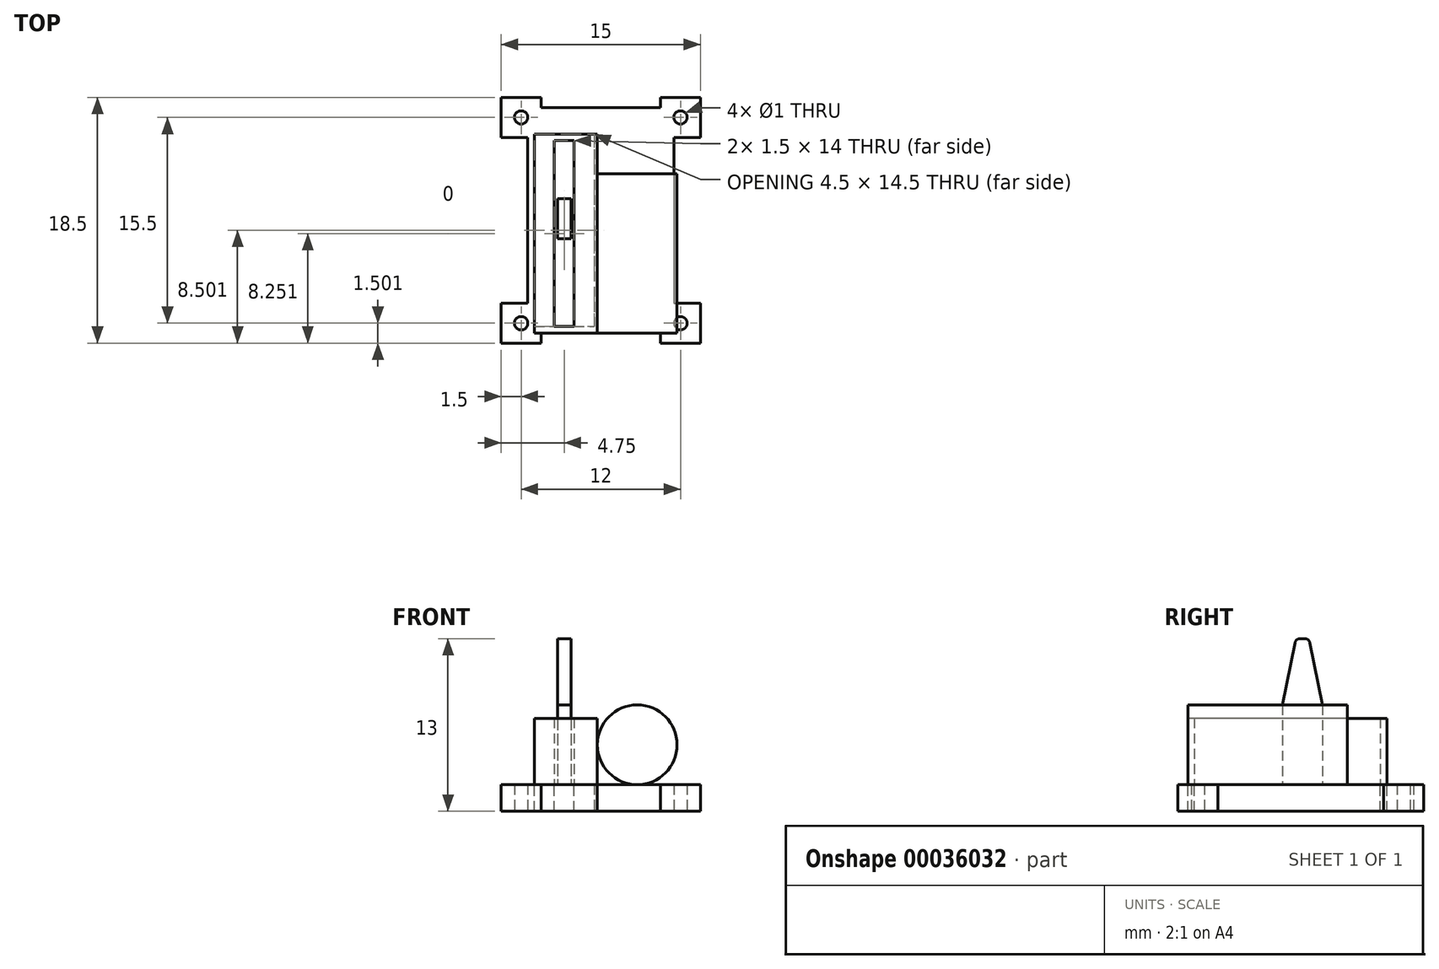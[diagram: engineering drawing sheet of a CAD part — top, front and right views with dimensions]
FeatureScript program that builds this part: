
annotation { "Feature Type Name" : "Feature", "Feature Type Description" : "" }
export const myFeature = defineFeature(function(context is Context, id is Id, definition is map)
    precondition{}
    {
        {
            var Q0;
            Q0=qCreatedBy(makeId("Top.planeOp"),FACE);
            var sketch = newSketch(context, id + "F0", { "sketchPlane" : qUnion([Q0])});
            skLineSegment(sketch, "E0.bottom", {"start": v(-5.24, 11.28) * mm, "end": v(5.76, 11.28) * mm, "construction": true});
            skLineSegment(sketch, "E0.top", {"start": v(-5.24, -5.72) * mm, "end": v(5.76, -5.72) * mm, "construction": true});
            skLineSegment(sketch, "E0.left", {"start": v(-5.24, 11.28) * mm, "end": v(-5.24, -5.22) * mm, "construction": true});
            skLineSegment(sketch, "E0.right", {"start": v(5.76, 11.28) * mm, "end": v(5.76, -5.72) * mm, "construction": true});
            skLineSegment(sketch, "E1.bottom", {"start": v(-7.24, 12.03) * mm, "end": v(7.76, 12.03) * mm, "construction": true});
            skLineSegment(sketch, "E1.top", {"start": v(-7.24, -6.47) * mm, "end": v(7.76, -6.47) * mm, "construction": true});
            skLineSegment(sketch, "E1.left", {"start": v(-7.24, 12.03) * mm, "end": v(-7.24, -6.47) * mm, "construction": true});
            skLineSegment(sketch, "E1.right", {"start": v(7.76, 12.03) * mm, "end": v(7.76, -6.47) * mm, "construction": true});
            skLineSegment(sketch, "E2.bottom", {"start": v(7.76, 12.03) * mm, "end": v(4.76, 12.03) * mm, "construction": true});
            skLineSegment(sketch, "E2.top", {"start": v(7.76, 9.03) * mm, "end": v(4.76, 9.03) * mm, "construction": true});
            skLineSegment(sketch, "E2.left", {"start": v(7.76, 12.03) * mm, "end": v(7.76, 9.03) * mm, "construction": true});
            skLineSegment(sketch, "E2.right", {"start": v(4.76, 12.03) * mm, "end": v(4.76, 9.03) * mm, "construction": true});
            skLineSegment(sketch, "E3.bottom", {"start": v(-7.24, 12.03) * mm, "end": v(-4.24, 12.03) * mm, "construction": true});
            skLineSegment(sketch, "E3.top", {"start": v(-7.24, 9.03) * mm, "end": v(-4.24, 9.03) * mm, "construction": true});
            skLineSegment(sketch, "E3.left", {"start": v(-7.24, 12.03) * mm, "end": v(-7.24, 9.03) * mm, "construction": true});
            skLineSegment(sketch, "E3.right", {"start": v(-4.24, 12.03) * mm, "end": v(-4.24, 9.03) * mm, "construction": true});
            skLineSegment(sketch, "E4.bottom", {"start": v(-7.24, -6.47) * mm, "end": v(-4.24, -6.47) * mm, "construction": true});
            skLineSegment(sketch, "E4.top", {"start": v(-7.24, -3.47) * mm, "end": v(-4.24, -3.47) * mm, "construction": true});
            skLineSegment(sketch, "E4.left", {"start": v(-7.24, -6.47) * mm, "end": v(-7.24, -3.47) * mm, "construction": true});
            skLineSegment(sketch, "E4.right", {"start": v(-4.24, -6.47) * mm, "end": v(-4.24, -3.47) * mm, "construction": true});
            skLineSegment(sketch, "E5.bottom", {"start": v(7.76, -6.47) * mm, "end": v(4.76, -6.47) * mm, "construction": true});
            skLineSegment(sketch, "E5.top", {"start": v(7.76, -3.47) * mm, "end": v(4.76, -3.47) * mm, "construction": true});
            skLineSegment(sketch, "E5.left", {"start": v(7.76, -6.47) * mm, "end": v(7.76, -3.47) * mm, "construction": true});
            skLineSegment(sketch, "E5.right", {"start": v(4.76, -6.47) * mm, "end": v(4.76, -3.47) * mm, "construction": true});
            skLineSegment(sketch, "E6", {"start": v(-7.24, 12.03) * mm, "end": v(-4.24, 12.03) * mm});
            skLineSegment(sketch, "E7", {"start": v(-4.24, 11.28) * mm, "end": v(4.76, 11.28) * mm});
            skLineSegment(sketch, "E8", {"start": v(4.76, 11.28) * mm, "end": v(4.76, 12.03) * mm});
            skLineSegment(sketch, "E9", {"start": v(7.76, 12.03) * mm, "end": v(7.76, 9.03) * mm});
            skLineSegment(sketch, "E10", {"start": v(4.76, 12.03) * mm, "end": v(7.76, 12.03) * mm});
            skLineSegment(sketch, "E11", {"start": v(7.76, 9.03) * mm, "end": v(5.76, 9.03) * mm});
            skLineSegment(sketch, "E12", {"start": v(5.76, 9.03) * mm, "end": v(5.76, -3.47) * mm});
            skLineSegment(sketch, "E13", {"start": v(5.76, -3.47) * mm, "end": v(7.76, -3.47) * mm});
            skLineSegment(sketch, "E14", {"start": v(7.76, -3.47) * mm, "end": v(7.76, -6.47) * mm});
            skLineSegment(sketch, "E15", {"start": v(7.76, -6.47) * mm, "end": v(4.76, -6.47) * mm});
            skLineSegment(sketch, "E16", {"start": v(4.76, -5.72) * mm, "end": v(4.76, -6.47) * mm});
            skLineSegment(sketch, "E17", {"start": v(4.76, -5.72) * mm, "end": v(-4.24, -5.72) * mm});
            skLineSegment(sketch, "E18", {"start": v(-4.24, -6.47) * mm, "end": v(-4.24, -5.72) * mm});
            skLineSegment(sketch, "E19", {"start": v(-4.24, -6.47) * mm, "end": v(-7.24, -6.47) * mm});
            skLineSegment(sketch, "E20", {"start": v(-7.24, -3.47) * mm, "end": v(-7.24, -6.47) * mm});
            skLineSegment(sketch, "E21", {"start": v(-7.24, -3.47) * mm, "end": v(-5.24, -3.47) * mm});
            skLineSegment(sketch, "E22", {"start": v(-5.24, -3.47) * mm, "end": v(-5.24, 9.03) * mm});
            skLineSegment(sketch, "E23", {"start": v(-5.24, 9.03) * mm, "end": v(-7.24, 9.03) * mm});
            skLineSegment(sketch, "E24", {"start": v(-7.24, 12.03) * mm, "end": v(-7.24, 9.03) * mm});
            skLineSegment(sketch, "E25", {"start": v(-4.24, 12.03) * mm, "end": v(-4.24, 11.28) * mm});
            skLineSegment(sketch, "E26", {"start": v(7.76, 12.03) * mm, "end": v(4.76, 9.03) * mm, "construction": true});
            skLineSegment(sketch, "E27", {"start": v(-7.24, 12.03) * mm, "end": v(-4.24, 9.03) * mm, "construction": true});
            skLineSegment(sketch, "E28", {"start": v(-4.24, -3.47) * mm, "end": v(-7.24, -6.47) * mm, "construction": true});
            skLineSegment(sketch, "E29", {"start": v(4.76, -3.47) * mm, "end": v(7.76, -6.47) * mm, "construction": true});
            skCircle(sketch, "E30", {"center": v(6.26, 10.53) * mm, "radius": 0.5 * mm});
            skCircle(sketch, "E31", {"center": v(-5.74, 10.53) * mm, "radius": 0.5 * mm});
            skCircle(sketch, "E32", {"center": v(6.26, -4.97) * mm, "radius": 0.5 * mm});
            skCircle(sketch, "E33", {"center": v(-5.74, -4.97) * mm, "radius": 0.5 * mm});
            skLineSegment(sketch, "E34.bottom", {"start": v(-4.74, 9.28) * mm, "end": v(-0.24, 9.28) * mm});
            skLineSegment(sketch, "E34.top", {"start": v(-4.74, -5.72) * mm, "end": v(-0.24, -5.72) * mm});
            skLineSegment(sketch, "E34.left", {"start": v(-4.74, 9.28) * mm, "end": v(-4.74, -5.72) * mm});
            skLineSegment(sketch, "E34.right", {"start": v(-0.24, 9.28) * mm, "end": v(-0.24, -5.72) * mm});
            skLineSegment(sketch, "E35.bottom", {"start": v(-3.24, 8.78) * mm, "end": v(-1.74, 8.78) * mm});
            skLineSegment(sketch, "E35.top", {"start": v(-3.24, -5.22) * mm, "end": v(-1.74, -5.22) * mm});
            skLineSegment(sketch, "E35.left", {"start": v(-3.24, 8.78) * mm, "end": v(-3.24, -5.22) * mm});
            skLineSegment(sketch, "E35.right", {"start": v(-1.74, 8.78) * mm, "end": v(-1.74, -5.22) * mm});
            skLineSegment(sketch, "E36", {"start": v(-4.74, -5.22) * mm, "end": v(-0.24, -5.22) * mm});
            skSolve(sketch);
        }
        {
            var Q0;
            {var subQ7=sQuery(id+"F0.wireOp",EDGE,"E34.top");var subQ10=makeQuery(id+"F0.imprint","INTERSECT",VERTEX,{"derivedFrom":[sQuery(id+"F0.wireOp",EDGE,"E18"),subQ7]});Q0=makeQuery(id+"F0.imprint","IMPRINT",FACE,{"disambiguationData":[TD([[makeQuery(id+"F0.imprint","IMPRINT",EDGE,{"disambiguationData":[TD([[subQ10,1.0]])],"derivedFrom":subQ7}),1.0]])]});}
            var Q1;
            Q1=makeQuery(id+"F0.imprint","IMPRINT",FACE,{"disambiguationData":[TD([[makeQuery(id+"F0.imprint","IMPRINT",EDGE,{"derivedFrom":sQuery(id+"F0.wireOp",EDGE,"E6")}),-1.0]])]});
            var Q2;
            Q2=makeQuery(id+"F0.imprint","IMPRINT",FACE,{"disambiguationData":[TD([[makeQuery(id+"F0.imprint","IMPRINT",EDGE,{"derivedFrom":sQuery(id+"F0.wireOp",EDGE,"E35.bottom")}),-1.0]])]});
            extrude(context, id + "F1", {"entities" : qUnion([Q0, Q1, Q2]), "depth" : 2 * mm});
        }
        {
            var Q0;
            Q0=makeQuery(id+"F1.opExtrude","CAP_FACE",FACE,{"disambiguationData":[OSD([sQuery(id+"F0.wireOp",EDGE,"E6"),sQuery(id+"F0.wireOp",EDGE,"E7"),sQuery(id+"F0.wireOp",EDGE,"E8"),sQuery(id+"F0.wireOp",EDGE,"E9"),sQuery(id+"F0.wireOp",EDGE,"E10"),sQuery(id+"F0.wireOp",EDGE,"E11"),sQuery(id+"F0.wireOp",EDGE,"E12"),sQuery(id+"F0.wireOp",EDGE,"E13"),sQuery(id+"F0.wireOp",EDGE,"E14"),sQuery(id+"F0.wireOp",EDGE,"E15"),sQuery(id+"F0.wireOp",EDGE,"E16"),sQuery(id+"F0.wireOp",EDGE,"E17"),sQuery(id+"F0.wireOp",EDGE,"E18"),sQuery(id+"F0.wireOp",EDGE,"E19"),sQuery(id+"F0.wireOp",EDGE,"E20"),sQuery(id+"F0.wireOp",EDGE,"E21"),sQuery(id+"F0.wireOp",EDGE,"E22"),sQuery(id+"F0.wireOp",EDGE,"E23"),sQuery(id+"F0.wireOp",EDGE,"E24"),sQuery(id+"F0.wireOp",EDGE,"E25"),sQuery(id+"F0.wireOp",EDGE,"E30"),sQuery(id+"F0.wireOp",EDGE,"E31"),sQuery(id+"F0.wireOp",EDGE,"E32"),sQuery(id+"F0.wireOp",EDGE,"E33"),sQuery(id+"F0.wireOp",EDGE,"E34.top")])],"isStart":false});
            var sketch = newSketch(context, id + "F2", { "sketchPlane" : qUnion([Q0])});
            skLineSegment(sketch, "E37.bottom", {"start": v(-4.74, 9.28) * mm, "end": v(0, 9.28) * mm});
            skLineSegment(sketch, "E37.top", {"start": v(-4.74, -5.72) * mm, "end": v(0, -5.72) * mm});
            skLineSegment(sketch, "E37.left", {"start": v(-4.74, 9.28) * mm, "end": v(-4.74, -5.72) * mm});
            skLineSegment(sketch, "E37.right", {"start": v(0, 9.28) * mm, "end": v(0, -5.72) * mm});
            skLineSegment(sketch, "E38.bottom", {"start": v(-3.24, 8.78) * mm, "end": v(-1.74, 8.78) * mm});
            skLineSegment(sketch, "E38.top", {"start": v(-3.24, -5.22) * mm, "end": v(-1.74, -5.22) * mm});
            skLineSegment(sketch, "E38.left", {"start": v(-3.24, 8.78) * mm, "end": v(-3.24, -5.22) * mm});
            skLineSegment(sketch, "E38.right", {"start": v(-1.74, 8.78) * mm, "end": v(-1.74, -5.22) * mm});
            skLineSegment(sketch, "E39.bottom", {"start": v(-2.99, 4.41) * mm, "end": v(-1.99, 4.41) * mm});
            skLineSegment(sketch, "E39.top", {"start": v(-2.99, 1.41) * mm, "end": v(-1.99, 1.41) * mm});
            skLineSegment(sketch, "E39.left", {"start": v(-2.99, 4.41) * mm, "end": v(-2.99, 1.41) * mm});
            skLineSegment(sketch, "E39.right", {"start": v(-1.99, 4.41) * mm, "end": v(-1.99, 1.41) * mm});
            skSolve(sketch);
        }
        {
            var Q0;
            Q0=makeQuery(id+"F2.imprint","IMPRINT",FACE,{"disambiguationData":[TD([[makeQuery(id+"F2.imprint","IMPRINT",EDGE,{"derivedFrom":sQuery(id+"F2.wireOp",EDGE,"E38.bottom")}),1.0]])]});
            var Q1;
            {var subQ7=sQuery(id+"F2.wireOp",EDGE,"E37.right");Q1=makeQuery(id+"F2.imprint","IMPRINT",FACE,{"disambiguationData":[TD([[makeQuery(id+"F2.imprint","IMPRINT",EDGE,{"derivedFrom":subQ7}),-1.0]])]});}
            extrude(context, id + "F3", {"entities" : qUnion([Q0, Q1]), "depth" : 5 * mm});
        }
        {
            var Q0;
            Q0=makeQuery(id+"F3.opExtrude","CAP_FACE",FACE,{"disambiguationData":[OSD([sQuery(id+"F2.wireOp",EDGE,"E37.bottom"),sQuery(id+"F2.wireOp",EDGE,"E37.top"),sQuery(id+"F2.wireOp",EDGE,"E37.left"),sQuery(id+"F2.wireOp",EDGE,"E37.right"),sQuery(id+"F2.wireOp",EDGE,"E38.bottom"),sQuery(id+"F2.wireOp",EDGE,"E38.top"),sQuery(id+"F2.wireOp",EDGE,"E38.left"),sQuery(id+"F2.wireOp",EDGE,"E38.right")])],"isStart":true});
            extrude(context, id + "F4", {"entities" : qUnion([Q0]), "depth" : 2 * mm});
        }
        {
            var Q0;
            Q0=makeQuery(id+"F3.opExtrude","SWEPT_FACE",FACE,{"disambiguationData":[OSD([sQuery(id+"F2.wireOp",EDGE,"E37.top")])]});
            var sketch = newSketch(context, id + "F5", { "sketchPlane" : qUnion([Q0])});
            skLineSegment(sketch, "E40", {"start": v(0, 2) * mm, "end": v(0, 5) * mm, "construction": true});
            skLineSegment(sketch, "E41", {"start": v(0, 5) * mm, "end": v(3, 5) * mm, "construction": true});
            skCircle(sketch, "E42", {"center": v(3, 5) * mm, "radius": 3 * mm});
            skSolve(sketch);
        }
        {
            var Q0;
            Q0 = qSketchRegion(id + "F5", true);
            extrude(context, id + "F6", {"entities" : qUnion([Q0]), "oppositeDirection" : true, "depth" : 12 * mm});
        }
        {
            var Q0;
            Q0=makeQuery(id+"F2.imprint","IMPRINT",FACE,{"disambiguationData":[TD([[makeQuery(id+"F2.imprint","IMPRINT",EDGE,{"derivedFrom":sQuery(id+"F2.wireOp",EDGE,"E39.bottom")}),-1.0]])]});
            extrude(context, id + "F7", {"entities" : qUnion([Q0]), "depth" : 11 * mm});
        }
        {
            var Q0;
            Q0=makeQuery(id+"F7.opExtrude","CAP_EDGE",EDGE,{"disambiguationData":[OSD([sQuery(id+"F2.wireOp",EDGE,"E39.top")])],"isStart":false});
            chamfer(context, id + "F8", {"entities" : qUnion([Q0]), "chamferType" : ChamferType.TWO_OFFSETS, "width1" : 1 * mm, "oppositeDirection" : false, "width2" : 5 * mm, "tangentPropagation" : true});
        }
        {
            var Q0;
            Q0=makeQuery(id+"F7.opExtrude","CAP_EDGE",EDGE,{"disambiguationData":[OSD([sQuery(id+"F2.wireOp",EDGE,"E39.bottom")])],"isStart":false});
            chamfer(context, id + "F9", {"entities" : qUnion([Q0]), "chamferType" : ChamferType.TWO_OFFSETS, "width1" : 1 * mm, "oppositeDirection" : true, "width2" : 5 * mm, "tangentPropagation" : true});
        }
        {
            var Q0;
            {var subQ0=sQuery(id+"F2.wireOp",EDGE,"E39.bottom");Q0=makeQuery(id+"F9.opChamfer","BLEND_EDGE",EDGE,{"blendedFrom":[makeQuery(id+"F7.opExtrude","CAP_EDGE",EDGE,{"disambiguationData":[OSD([subQ0])],"isStart":false}),makeQuery(id+"F7.opExtrude","CAP_FACE",FACE,{"disambiguationData":[OSD([subQ0,sQuery(id+"F2.wireOp",EDGE,"E39.top"),sQuery(id+"F2.wireOp",EDGE,"E39.left"),sQuery(id+"F2.wireOp",EDGE,"E39.right")])],"isStart":false})],"blendedInto":[makeQuery(id+"F7.opExtrude","CAP_FACE",FACE,{"disambiguationData":[OSD([subQ0,sQuery(id+"F2.wireOp",EDGE,"E39.top"),sQuery(id+"F2.wireOp",EDGE,"E39.left"),sQuery(id+"F2.wireOp",EDGE,"E39.right")])],"isStart":false})]});}
            var Q1;
            {var subQ0=sQuery(id+"F2.wireOp",EDGE,"E39.top");Q1=makeQuery(id+"F8.opChamfer","BLEND_EDGE",EDGE,{"blendedFrom":[makeQuery(id+"F7.opExtrude","CAP_EDGE",EDGE,{"disambiguationData":[OSD([subQ0])],"isStart":false}),makeQuery(id+"F7.opExtrude","CAP_FACE",FACE,{"disambiguationData":[OSD([sQuery(id+"F2.wireOp",EDGE,"E39.bottom"),subQ0,sQuery(id+"F2.wireOp",EDGE,"E39.left"),sQuery(id+"F2.wireOp",EDGE,"E39.right")])],"isStart":false})],"blendedInto":[makeQuery(id+"F7.opExtrude","CAP_FACE",FACE,{"disambiguationData":[OSD([sQuery(id+"F2.wireOp",EDGE,"E39.bottom"),subQ0,sQuery(id+"F2.wireOp",EDGE,"E39.left"),sQuery(id+"F2.wireOp",EDGE,"E39.right")])],"isStart":false})]});}
            fillet(context, id + "F10", {"entities" : qUnion([Q0, Q1]), "radius" : 0.4 * mm, "tangentPropagation" : true, "allowEdgeOverflow" : false});
        }
    });
